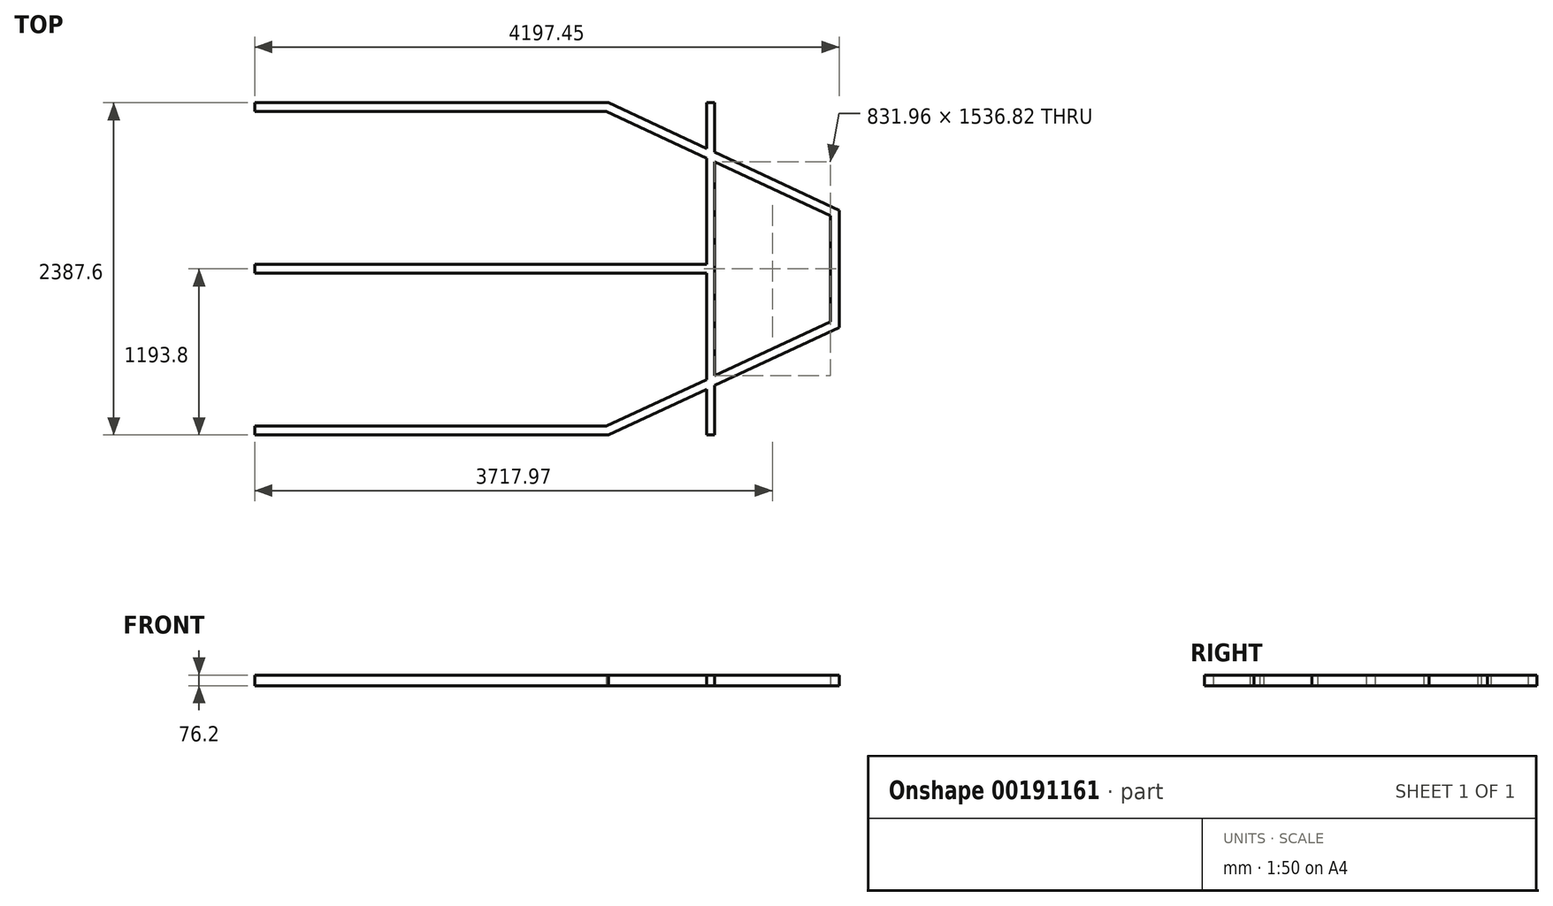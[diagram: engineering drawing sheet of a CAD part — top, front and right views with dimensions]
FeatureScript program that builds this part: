
annotation { "Feature Type Name" : "Feature", "Feature Type Description" : "" }
export const myFeature = defineFeature(function(context is Context, id is Id, definition is map)
    precondition{}
    {
        {
            var Q0;
            Q0=qCreatedBy(makeId("Top.planeOp"),FACE);
            var sketch = newSketch(context, id + "F0", { "sketchPlane" : qUnion([Q0])});
            skLineSegment(sketch, "E0.bottom", {"start": v(-788.63, 2163.82) * mm, "end": v(1751.37, 2163.82) * mm});
            skLineSegment(sketch, "E0.top", {"start": v(-788.63, 2100.32) * mm, "end": v(1751.37, 2100.32) * mm});
            skLineSegment(sketch, "E0.left", {"start": v(-788.63, 2163.82) * mm, "end": v(-788.63, 2100.32) * mm});
            skLineSegment(sketch, "E0.right", {"start": v(1751.37, 2163.82) * mm, "end": v(1751.37, 2100.32) * mm});
            skLineSegment(sketch, "E1.bottom", {"start": v(-788.63, -160.28) * mm, "end": v(1751.37, -160.28) * mm});
            skLineSegment(sketch, "E1.top", {"start": v(-788.63, -223.78) * mm, "end": v(1751.37, -223.78) * mm});
            skLineSegment(sketch, "E1.left", {"start": v(-788.63, -160.28) * mm, "end": v(-788.63, -223.78) * mm});
            skLineSegment(sketch, "E1.right", {"start": v(1751.37, -160.28) * mm, "end": v(1751.37, -223.78) * mm});
            skLineSegment(sketch, "E2.bottom", {"start": v(-788.63, 1001.77) * mm, "end": v(2513.37, 1001.77) * mm});
            skLineSegment(sketch, "E2.top", {"start": v(-788.63, 938.27) * mm, "end": v(2513.37, 938.27) * mm});
            skLineSegment(sketch, "E2.left", {"start": v(-788.63, 1001.77) * mm, "end": v(-788.63, 938.27) * mm});
            skLineSegment(sketch, "E2.right", {"start": v(2513.37, 1001.77) * mm, "end": v(2513.37, 938.27) * mm});
            skLineSegment(sketch, "E3", {"start": v(1751.37, 2163.82) * mm, "end": v(3408.82, 1390.94) * mm});
            skLineSegment(sketch, "E4", {"start": v(1751.37, -223.78) * mm, "end": v(3408.82, 549.1) * mm});
            skLineSegment(sketch, "E5", {"start": v(1737.29, -160.28) * mm, "end": v(3486.82, 655.54) * mm});
            skLineSegment(sketch, "E6", {"start": v(1737.29, 2100.32) * mm, "end": v(3446.29, 1303.4) * mm});
            skLineSegment(sketch, "E7", {"start": v(3408.82, 1390.94) * mm, "end": v(3408.82, 549.1) * mm});
            skLineSegment(sketch, "E8", {"start": v(3345.32, 519.5) * mm, "end": v(3345.32, 1420.55) * mm});
            skLineSegment(sketch, "E9.bottom", {"start": v(2513.37, 2163.82) * mm, "end": v(2455.7, 2163.82) * mm});
            skLineSegment(sketch, "E9.top", {"start": v(2513.37, -223.78) * mm, "end": v(2455.7, -223.78) * mm});
            skLineSegment(sketch, "E9.left", {"start": v(2513.37, 2163.82) * mm, "end": v(2513.37, -223.78) * mm});
            skLineSegment(sketch, "E9.right", {"start": v(2455.7, 2163.82) * mm, "end": v(2455.7, -223.78) * mm});
            skSolve(sketch);
        }
        {
            var Q0;
            Q0 = qSketchRegion(id + "F0", true);
            extrude(context, id + "F1", {"entities" : qUnion([Q0]), "depth" : 76.2 * mm});
        }
    });
